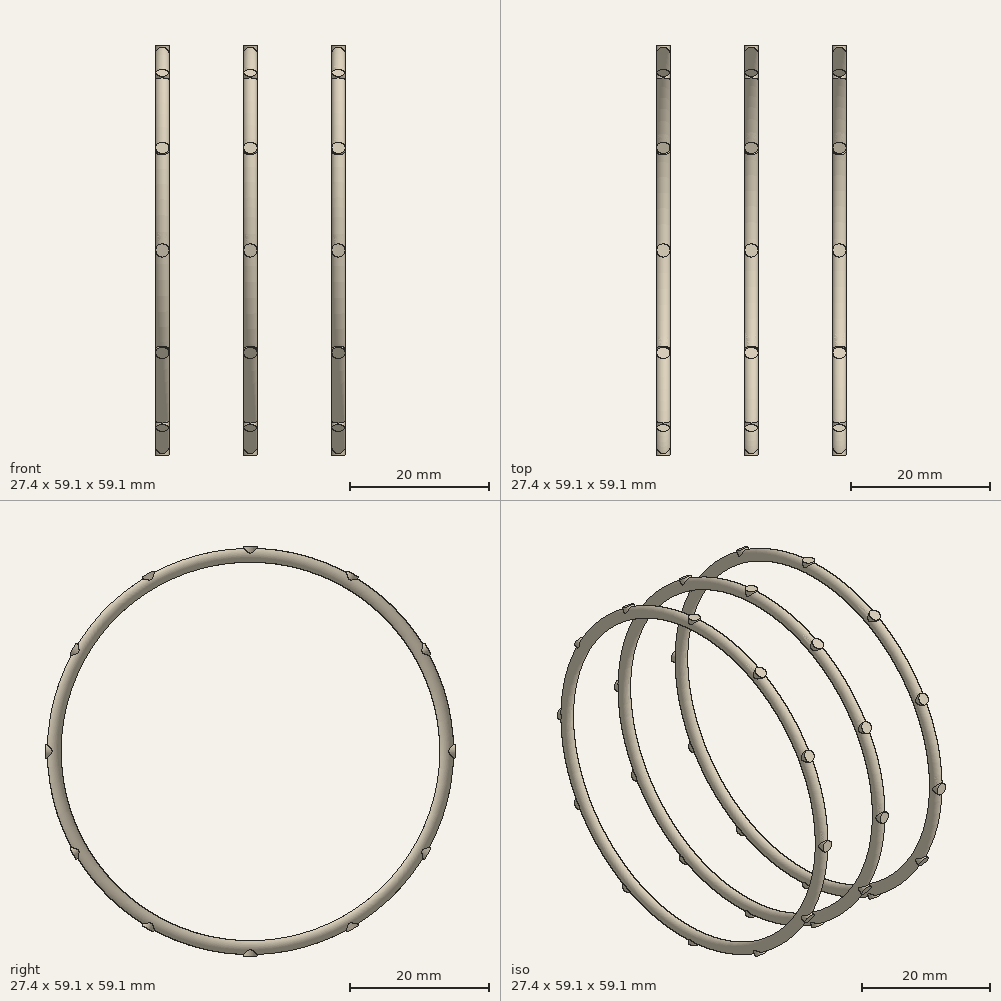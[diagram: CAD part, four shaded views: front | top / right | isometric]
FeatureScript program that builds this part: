
annotation { "Feature Type Name" : "Feature", "Feature Type Description" : "" }
export const myFeature = defineFeature(function(context is Context, id is Id, definition is map)
    precondition{}
    {
        {
            var Q0;
            Q0=qCreatedBy(makeId("Front.planeOp"),FACE);
            var sketch = newSketch(context, id + "F0", { "sketchPlane" : qUnion([Q0])});
            skCircle(sketch, "E0", {"center": v(0, 0) * mm, "radius": 1 * mm});
            skSolve(sketch);
        }
        {
            var Q0;
            Q0=qCreatedBy(makeId("Front.planeOp"),FACE);
            var sketch = newSketch(context, id + "F1", { "sketchPlane" : qUnion([Q0])});
            skLineSegment(sketch, "E1", {"start": v(-163.33, -28.3) * mm, "end": v(162.23, -28.3) * mm});
            skSolve(sketch);
        }
        {
            var Q0;
            Q0=makeQuery(id+"F0.imprint","IMPRINT",FACE,{"disambiguationData":[TD([[makeQuery(id+"F0.imprint","IMPRINT",EDGE,{"derivedFrom":sQuery(id+"F0.wireOp",EDGE,"E0")}),1.0]])]});
            var Q1;
            Q1=sQuery(id+"F1.wireOp",EDGE,"E1");
            revolve(context, id + "F2", {"entities" : qUnion([Q0]), "axis" : qUnion([Q1]), "revolveType" : RevolveType.FULL});
        }
        {
            var Q0;
            Q0=qCreatedBy(makeId("Top.planeOp"),FACE);
            var sketch = newSketch(context, id + "F3", { "sketchPlane" : qUnion([Q0])});
            skCircle(sketch, "E2", {"center": v(0, 0) * mm, "radius": 0.95 * mm});
            skSolve(sketch);
        }
        {
            var Q0;
            Q0 = qSketchRegion(id + "F3", true);
            extrude(context, id + "F4", {"entities" : qUnion([Q0]), "operationType" : NewBodyOperationType.ADD, "depth" : 1.27 * mm});
        }
        {
            var Q0;
            Q0=makeQuery(id+"F4.opExtrude","CAP_FACE",FACE,{"disambiguationData":[OSD([sQuery(id+"F3.wireOp",EDGE,"E2")])],"isStart":false});
            var Q1;
            Q1=makeQuery(id+"F4.opExtrude","SWEPT_FACE",FACE,{"disambiguationData":[OSD([sQuery(id+"F3.wireOp",EDGE,"E2")])]});
            var Q2;
            Q2=sQuery(id+"F1.wireOp",EDGE,"E1");
            circularPattern(context, id + "F5", {"faces" : qUnion([Q0, Q1]), "axis" : qUnion([Q2]), "angle" : 30 * degree, "instanceCount" : 12, "patternType" : PatternType.FACE});
        }
        {
            var Q0;
            Q0=makeQuery(id+"F2.opRevolve","SWEPT_BODY",BODY,{"disambiguationData":[OSD([sQuery(id+"F0.wireOp",EDGE,"E0")])]});
            transform(context, id + "F6", {"entities" : qUnion([Q0]), "transformType" : TransformType.TRANSLATION_3D, "dx" : 12.7 * mm, "dy" : 0 * mm, "dz" : 0 * mm, "makeCopy" : true});
        }
        {
            var Q0;
            Q0=makeQuery(id+"F2.opRevolve","SWEPT_BODY",BODY,{"disambiguationData":[OSD([sQuery(id+"F0.wireOp",EDGE,"E0")])]});
            transform(context, id + "F7", {"entities" : qUnion([Q0]), "transformType" : TransformType.TRANSLATION_3D, "dx" : 25.4 * mm, "dy" : 0 * mm, "dz" : 0 * mm, "makeCopy" : true});
        }
        {
            var Q0;
            Q0=qCreatedBy(makeId("Right.planeOp"),FACE);
            var sketch = newSketch(context, id + "F8", { "sketchPlane" : qUnion([Q0])});
            skCircle(sketch, "E3", {"center": v(0, 0) * mm, "radius": 0.64 * mm});
            skSolve(sketch);
        }
        {
            var Q0;
            Q0=sQuery(id+"F8.wireOp",EDGE,"E3");
            extrude(context, id + "F9", {"bodyType" : ToolBodyType.SURFACE, "surfaceEntities" : qUnion([Q0]), "depth" : 12.7 * mm});
        }
        {
            var Q0;
            Q0=makeQuery(id+"F9.opExtrude","SWEPT_BODY",BODY,{"disambiguationData":[OSD([sQuery(id+"F8.wireOp",EDGE,"E3")])]});
            var Q1;
            Q1=sQuery(id+"F1.wireOp",EDGE,"E1");
            circularPattern(context, id + "F10", {"entities" : qUnion([Q0]), "axis" : qUnion([Q1]), "angle" : 60 * degree, "instanceCount" : 6});
        }
    });
